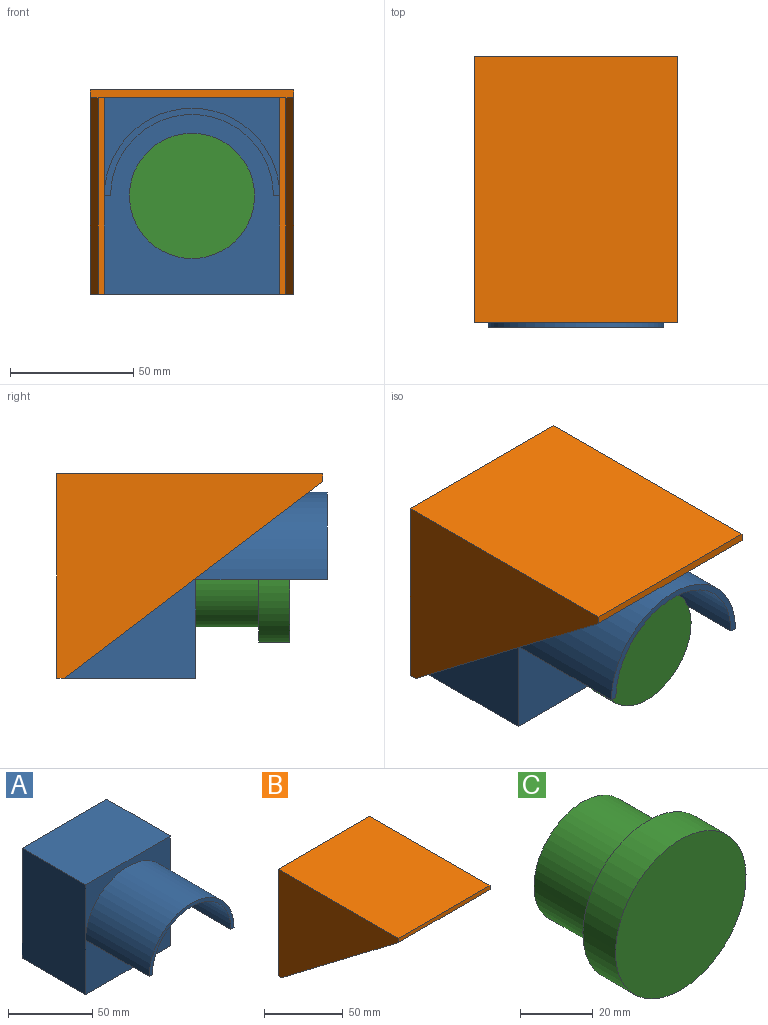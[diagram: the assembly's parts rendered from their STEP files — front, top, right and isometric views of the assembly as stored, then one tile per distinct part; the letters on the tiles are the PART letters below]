
ASSEMBLY  parts=3 mates=2
PART A: 17 faces, bbox 71.1x106.7x79.8 mm
  f0: plane 79.76x71.12mm, normal (0,1,0), area 2769mm2, adj f2,f3,f4,f5,f12,f13,f14,f15
  f1: plane 71.12x39.88mm, normal (0,-1,0), area 849.8mm2, adj f2,f3,f5,f10
  f2: plane 71.12x53.34mm, normal (0,0,1), area 3793.5mm2, adj f0,f1,f3,f5
  f3: plane 79.76x53.34mm, normal (-1,0,0), area 4254.2mm2, adj f0,f1,f2,f4,f6
  f4: plane 71.12x53.34mm, normal (0,0,-1), area 3793.5mm2, adj f0,f3,f5,f6
  f5: plane 79.76x53.34mm, normal (1,0,0), area 4254.2mm2, adj f0,f1,f2,f4,f6
  f6: plane 72.9x71.12mm, normal (0,-1,0), area 4548.8mm2, adj f3,f4,f5,f7,f8,f9
  f7: plane 53.34x2.54mm, normal (0,0,-1), area 135.5mm2, adj f6,f8,f10,f11
  f8: cylinder r=33.02mm len=66.04mm, axis (0,1,0), area 5533.2mm2, adj f6,f7,f9,f11
  f9: plane 53.34x2.54mm, normal (0,0,-1), area 135.5mm2, adj f6,f8,f10,f11
  f10: cylinder r=35.56mm len=71.12mm, axis (0,1,0), area 5958.9mm2, adj f1,f7,f9,f11
  f11: plane 71.12x35.56mm, normal (0,-1,0), area 273.6mm2, adj f7,f8,f9,f10
  f12: plane 57.15x44.45mm, normal (1,0,0), area 2540.3mm2, adj f0,f13,f15,f16
  f13: plane 50.8x44.45mm, normal (0,0,-1), area 2258.1mm2, adj f0,f12,f14,f16
  f14: plane 57.15x44.45mm, normal (-1,0,0), area 2540.3mm2, adj f0,f13,f15,f16
  f15: plane 50.8x44.45mm, normal (0,0,1), area 2258.1mm2, adj f0,f12,f14,f16
  f16: plane 57.15x50.8mm, normal (0,1,0), area 2903.2mm2, adj f12,f13,f14,f15
PART B: 12 faces, bbox 82.6x108x82.9 mm
  f0: plane 82.55x3.18mm, normal (0,0,-1), area 262.1mm2, adj f1,f2,f7,f8,f9,f10
  f1: plane 79.76x76.2mm, normal (0,-1,0), area 6077.4mm2, adj f0,f3,f6,f11
  f2: plane 82.93x82.55mm, normal (0,1,0), area 6846mm2, adj f0,f5,f8,f10
  f3: plane 104.78x76.2mm, normal (0,0,-1), area 7983.9mm2, adj f1,f4,f6,f11
  f4: plane 82.55x3.18mm, normal (0,-1,0), area 262.1mm2, adj f3,f5,f7,f8,f9,f10
  f5: plane 107.95x82.55mm, normal (0,0,1), area 8911.3mm2, adj f2,f4,f8,f10
  f6: plane 104.78x79.76mm, normal (-1,0,0), area 4178.2mm2, adj f1,f3,f7
  f7: plane 104.78x79.76mm, normal (0,-0.61,-0.8), area 418.1mm2, adj f0,f4,f6,f8
  f8: plane 107.95x82.93mm, normal (1,0,0), area 4774.2mm2, adj f0,f2,f4,f5,f7
  f9: plane 104.78x79.76mm, normal (0,-0.61,-0.8), area 418.1mm2, adj f0,f4,f10,f11
  f10: plane 107.95x82.93mm, normal (-1,0,0), area 4774.2mm2, adj f0,f2,f4,f5,f9
  f11: plane 104.78x79.76mm, normal (1,0,0), area 4178.2mm2, adj f1,f3,f9
PART C: 5 faces, bbox 50.8x38.1x50.8 mm
  f0: cylinder r=19.05mm len=38.1mm, axis (0,1,0), area 3040.2mm2, adj f1,f4
  f1: plane 38.1x38.1mm, normal (0,1,0), area 1140.1mm2, adj f0
  f2: cylinder r=25.4mm len=50.8mm, axis (0,1,0), area 2026.8mm2, adj f3,f4
  f3: plane 50.8x50.8mm, normal (0,-1,0), area 2026.8mm2, adj f2
  f4: plane 50.8x50.8mm, normal (0,1,0), area 886.7mm2, adj f0,f2
PLACE A t=(0,-386.84,0)mm
PLACE B t=(0,-383.67,0)mm
PLACE C t=(0,-440.18,0)mm
MATE fastened C.f0 <-> A.f8  axis (0,1,0) through (0,-440.18,0)mm
MATE fastened B.f1 <-> A.f0  axis (0,-1,0) through (0,-386.84,39.88)mm
